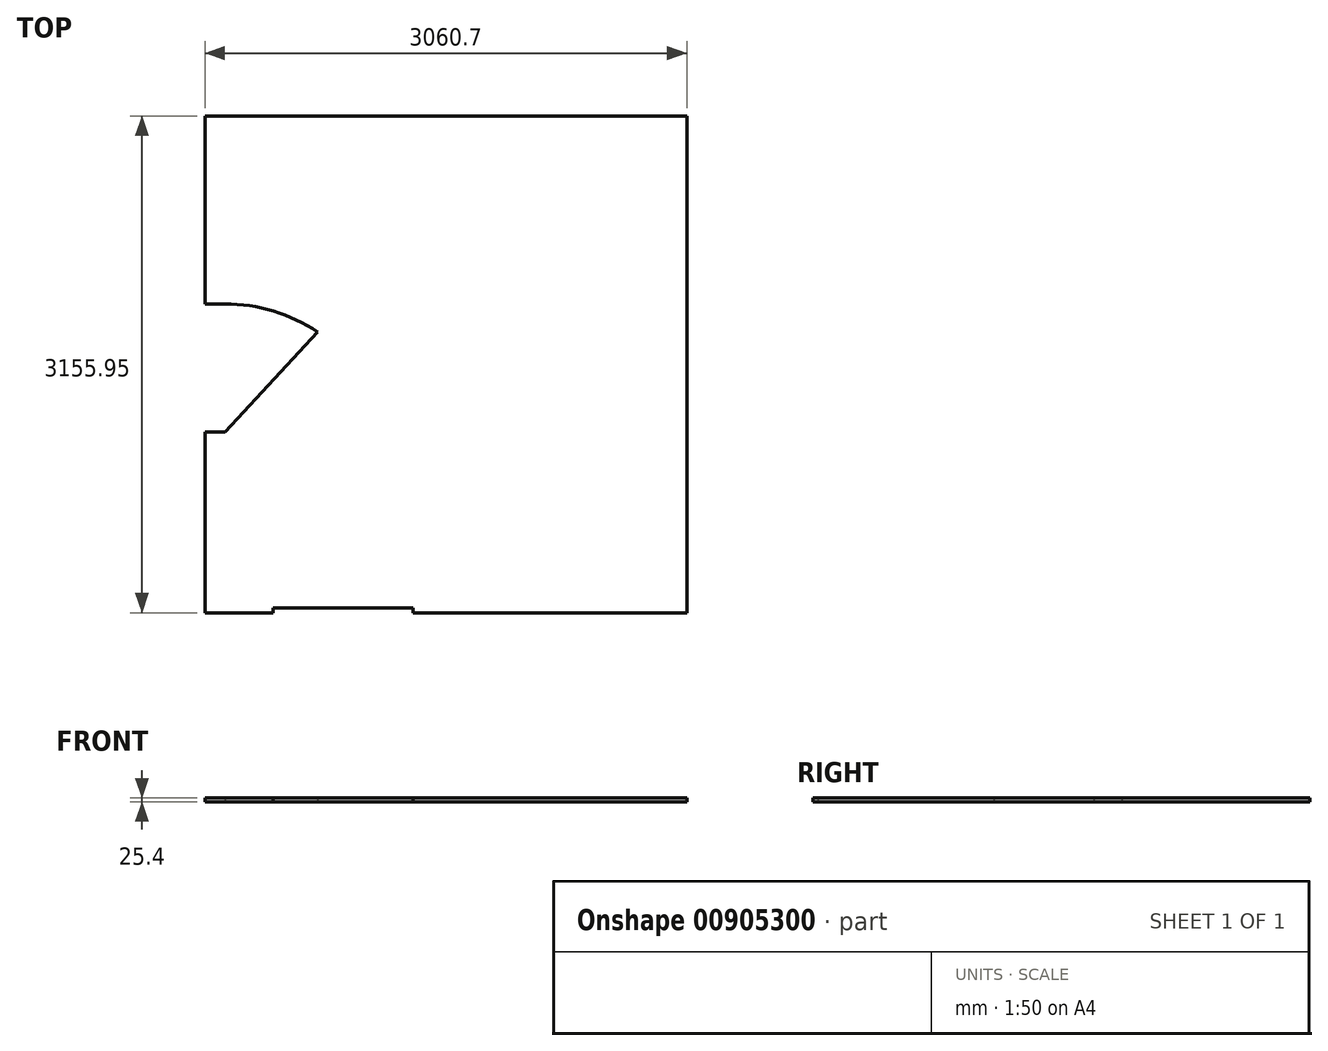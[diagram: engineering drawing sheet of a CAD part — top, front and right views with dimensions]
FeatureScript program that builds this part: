
annotation { "Feature Type Name" : "Feature", "Feature Type Description" : "" }
export const myFeature = defineFeature(function(context is Context, id is Id, definition is map)
    precondition{}
    {
        {
            var Q0;
            Q0=qCreatedBy(makeId("Top.planeOp"),FACE);
            var sketch = newSketch(context, id + "F0", { "sketchPlane" : qUnion([Q0])});
            skLineSegment(sketch, "E0.bottom", {"start": v(-2806.7, 2901.95) * mm, "end": v(0, 2901.95) * mm});
            skLineSegment(sketch, "E0.top", {"start": v(-2806.7, 0) * mm, "end": v(-2501.9, 0) * mm});
            skLineSegment(sketch, "E0.left", {"start": v(-2806.7, 2901.95) * mm, "end": v(-2806.7, 1835.15) * mm});
            skLineSegment(sketch, "E0.right", {"start": v(0, 2901.95) * mm, "end": v(0, 0) * mm});
            skLineSegment(sketch, "E1.0", {"start": v(-2933.7, 3028.95) * mm, "end": v(127, 3028.95) * mm});
            skLineSegment(sketch, "E1.1", {"start": v(-2933.7, 3028.95) * mm, "end": v(-2933.7, 1835.15) * mm});
            skLineSegment(sketch, "E1.2", {"start": v(-2933.7, -127) * mm, "end": v(-2501.9, -127) * mm});
            skLineSegment(sketch, "E1.3", {"start": v(127, 3028.95) * mm, "end": v(127, -127) * mm});
            skLineSegment(sketch, "E2", {"start": v(-2933.7, 1835.15) * mm, "end": v(-2806.7, 1835.15) * mm});
            skLineSegment(sketch, "E3", {"start": v(-2933.7, 1022.35) * mm, "end": v(-2806.7, 1022.35) * mm});
            skLineSegment(sketch, "E4", {"start": v(-1308.1, 0) * mm, "end": v(-1308.1, 990.6) * mm});
            skLineSegment(sketch, "E5", {"start": v(-1308.1, 990.6) * mm, "end": v(-1181.1, 990.6) * mm});
            skLineSegment(sketch, "E6", {"start": v(-1181.1, 990.6) * mm, "end": v(-1181.1, 0) * mm});
            skLineSegment(sketch, "E7.trimOffspring", {"start": v(-2806.7, 1022.35) * mm, "end": v(-2806.7, 0) * mm});
            skLineSegment(sketch, "E8.trimOffspring", {"start": v(-2933.7, 1022.35) * mm, "end": v(-2933.7, -127) * mm});
            skLineSegment(sketch, "E9.trimOffspring", {"start": v(-1181.1, 0) * mm, "end": v(0, 0) * mm});
            skLineSegment(sketch, "E10", {"start": v(-2501.9, 0) * mm, "end": v(-2501.9, -31.75) * mm});
            skLineSegment(sketch, "E11", {"start": v(-1612.9, 0) * mm, "end": v(-1612.9, -31.75) * mm});
            skLineSegment(sketch, "E12.trimOffspring", {"start": v(-1612.9, 0) * mm, "end": v(-1308.1, 0) * mm});
            skLineSegment(sketch, "E13.trimOffspring", {"start": v(-1612.9, -127) * mm, "end": v(127, -127) * mm});
            skLineSegment(sketch, "E14", {"start": v(-2501.9, -31.75) * mm, "end": v(-1612.9, -31.75) * mm});
            skLineSegment(sketch, "E15", {"start": v(-2501.9, -95.25) * mm, "end": v(-1612.9, -95.25) * mm});
            skLineSegment(sketch, "E16.trimOffspring", {"start": v(-2501.9, -95.25) * mm, "end": v(-2501.9, -127) * mm});
            skLineSegment(sketch, "E17.trimOffspring", {"start": v(-1612.9, -95.25) * mm, "end": v(-1612.9, -127) * mm});
            skLineSegment(sketch, "E18", {"start": v(-2501.9, -31.75) * mm, "end": v(-2501.9, -95.25) * mm, "construction": true});
            skLineSegment(sketch, "E19", {"start": v(-1612.9, -31.75) * mm, "end": v(-1612.9, -95.25) * mm, "construction": true});
            skLineSegment(sketch, "E20", {"start": v(-2501.9, 0) * mm, "end": v(-1612.9, 0) * mm, "construction": true});
            skLineSegment(sketch, "E21", {"start": v(-2501.9, -127) * mm, "end": v(-1612.9, -127) * mm, "construction": true});
            skLineSegment(sketch, "E22", {"start": v(-2806.7, 1022.35) * mm, "end": v(-2161.56, 1718.03) * mm});
            skArc(sketch, "E23", {"start": v(-2217.87, 1657.31) * mm, "mid": v(-2499.15, 1789.72) * mm, "end": v(-2806.7, 1835.15) * mm});
            skSolve(sketch);
        }
        {
            var Q0;
            Q0 = qSketchRegion(id + "F0", true);
            extrude(context, id + "F1", {"entities" : qUnion([Q0]), "depth" : 25.4 * mm, "offsetDistance" : 25.4 * mm});
        }
    });
